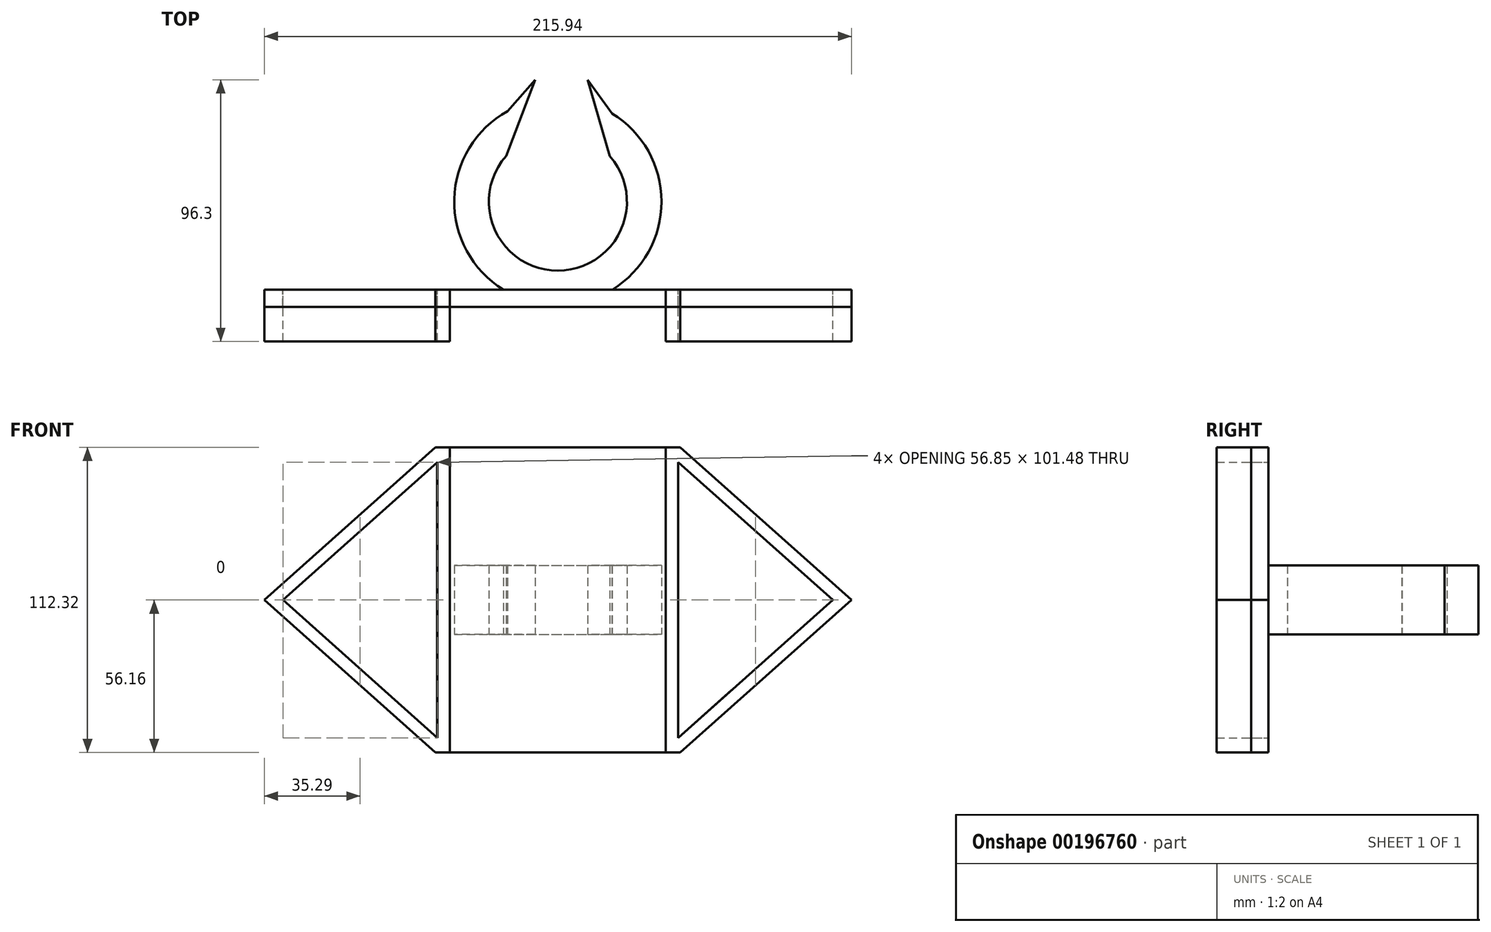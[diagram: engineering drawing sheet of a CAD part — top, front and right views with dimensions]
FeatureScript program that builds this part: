
annotation { "Feature Type Name" : "Feature", "Feature Type Description" : "" }
export const myFeature = defineFeature(function(context is Context, id is Id, definition is map)
    precondition{}
    {
        {
            var Q0;
            Q0=qCreatedBy(makeId("Front.planeOp"),FACE);
            var sketch = newSketch(context, id + "F0", { "sketchPlane" : qUnion([Q0])});
            skPoint(sketch, "E0.middle", {"position": v(0, 0) * mm});
            skLineSegment(sketch, "E1", {"start": v(44.25, 50.74) * mm, "end": v(101.1, 0) * mm});
            skLineSegment(sketch, "E2", {"start": v(101.1, 0) * mm, "end": v(44.25, -50.74) * mm});
            skLineSegment(sketch, "E3", {"start": v(-44.25, 50.74) * mm, "end": v(-101.1, 0) * mm});
            skLineSegment(sketch, "E4", {"start": v(-101.1, 0) * mm, "end": v(-44.25, -50.74) * mm});
            skLineSegment(sketch, "E5.bottom", {"start": v(-45.05, 56.16) * mm, "end": v(45.05, 56.16) * mm});
            skLineSegment(sketch, "E5.top", {"start": v(-45.05, -56.16) * mm, "end": v(45.05, -56.16) * mm});
            skLineSegment(sketch, "E6", {"start": v(-45.05, 56.16) * mm, "end": v(-107.97, 0) * mm});
            skLineSegment(sketch, "E7", {"start": v(-107.97, 0) * mm, "end": v(-45.05, -56.16) * mm});
            skLineSegment(sketch, "E8", {"start": v(45.05, -56.16) * mm, "end": v(107.97, 0) * mm});
            skLineSegment(sketch, "E9", {"start": v(107.97, 0) * mm, "end": v(45.05, 56.16) * mm});
            skLineSegment(sketch, "E10", {"start": v(-44.25, 50.74) * mm, "end": v(-44.25, -50.74) * mm});
            skLineSegment(sketch, "E11", {"start": v(44.25, 50.74) * mm, "end": v(44.25, -50.74) * mm});
            skLineSegment(sketch, "E12", {"start": v(-39.68, 56.16) * mm, "end": v(-39.68, -56.16) * mm});
            skLineSegment(sketch, "E13", {"start": v(39.68, 56.16) * mm, "end": v(39.68, -56.16) * mm});
            skSolve(sketch);
        }
        {
            var Q0;
            Q0=makeQuery(id+"F0.imprint","IMPRINT",FACE,{"disambiguationData":[TD([[makeQuery(id+"F0.imprint","IMPRINT",EDGE,{"derivedFrom":sQuery(id+"F0.wireOp",EDGE,"E1")}),1.0]])]});
            var Q1;
            Q1=makeQuery(id+"F0.imprint","IMPRINT",FACE,{"disambiguationData":[TD([[makeQuery(id+"F0.imprint","IMPRINT",EDGE,{"derivedFrom":sQuery(id+"F0.wireOp",EDGE,"E3")}),-1.0]])]});
            extrude(context, id + "F1", {"entities" : qUnion([Q0, Q1]), "depth" : 19.05 * mm});
        }
        {
            var Q0;
            Q0 = qSketchRegion(id + "F0", true);
            extrude(context, id + "F2", {"entities" : qUnion([Q0]), "depth" : 6.35 * mm});
        }
        {
            var Q0;
            Q0=qCreatedBy(makeId("Front.planeOp"),FACE);
            var sketch = newSketch(context, id + "F3", { "sketchPlane" : qUnion([Q0])});
            skPoint(sketch, "E14.middle", {"position": v(-0.05, 0) * mm});
            skLineSegment(sketch, "E15", {"start": v(44.26, 50.74) * mm, "end": v(101.1, 0) * mm});
            skLineSegment(sketch, "E16", {"start": v(101.1, 0) * mm, "end": v(44.25, -50.74) * mm});
            skLineSegment(sketch, "E17", {"start": v(-44.36, 50.74) * mm, "end": v(-101.2, 0) * mm});
            skLineSegment(sketch, "E18", {"start": v(-101.2, 0) * mm, "end": v(-44.36, -50.74) * mm});
            skLineSegment(sketch, "E19.top", {"start": v(-44.97, -55.92) * mm, "end": v(45.13, -55.92) * mm});
            skLineSegment(sketch, "E20", {"start": v(-44.36, 50.74) * mm, "end": v(-44.36, -50.74) * mm});
            skLineSegment(sketch, "E21", {"start": v(44.26, 50.74) * mm, "end": v(44.25, -50.74) * mm});
            skSolve(sketch);
        }
        {
            var Q0;
            Q0 = qSketchRegion(id + "F3", true);
            extrude(context, id + "F4", {"entities" : qUnion([Q0]), "depth" : 6.35 * mm});
        }
        {
            var Q0;
            Q0=qCreatedBy(makeId("Top.planeOp"),FACE);
            var sketch = newSketch(context, id + "F5", { "sketchPlane" : qUnion([Q0])});
            skArc(sketch, "E22", {"start": v(-19.08, 49.15) * mm, "mid": v(-0.02, 6.98) * mm, "end": v(19.1, 49.11) * mm});
            skArc(sketch, "E23", {"start": v(19.79, -0.18) * mm, "mid": v(38.1, 32.26) * mm, "end": v(20, 64.82) * mm});
            skLineSegment(sketch, "E24", {"start": v(-20.01, -0.04) * mm, "end": v(19.79, -0.18) * mm});
            skArc(sketch, "E25.trimOffspring", {"start": v(-18.5, 65.69) * mm, "mid": v(-38.09, 33.26) * mm, "end": v(-20.01, -0.04) * mm});
            skLineSegment(sketch, "E26", {"start": v(20, 64.82) * mm, "end": v(11, 77.25) * mm});
            skLineSegment(sketch, "E27", {"start": v(-8.41, 77.25) * mm, "end": v(-18.5, 65.69) * mm});
            skLineSegment(sketch, "E28", {"start": v(-8.41, 77.25) * mm, "end": v(-19.08, 49.15) * mm});
            skLineSegment(sketch, "E29", {"start": v(11, 77.25) * mm, "end": v(19.1, 49.11) * mm});
            skSolve(sketch);
        }
        {
            var Q0;
            Q0 = qSketchRegion(id + "F5", true);
            extrude(context, id + "F6", {"entities" : qUnion([Q0]), "endBound" : BoundingType.SYMMETRIC, "depth" : 25.4 * mm});
        }
    });
